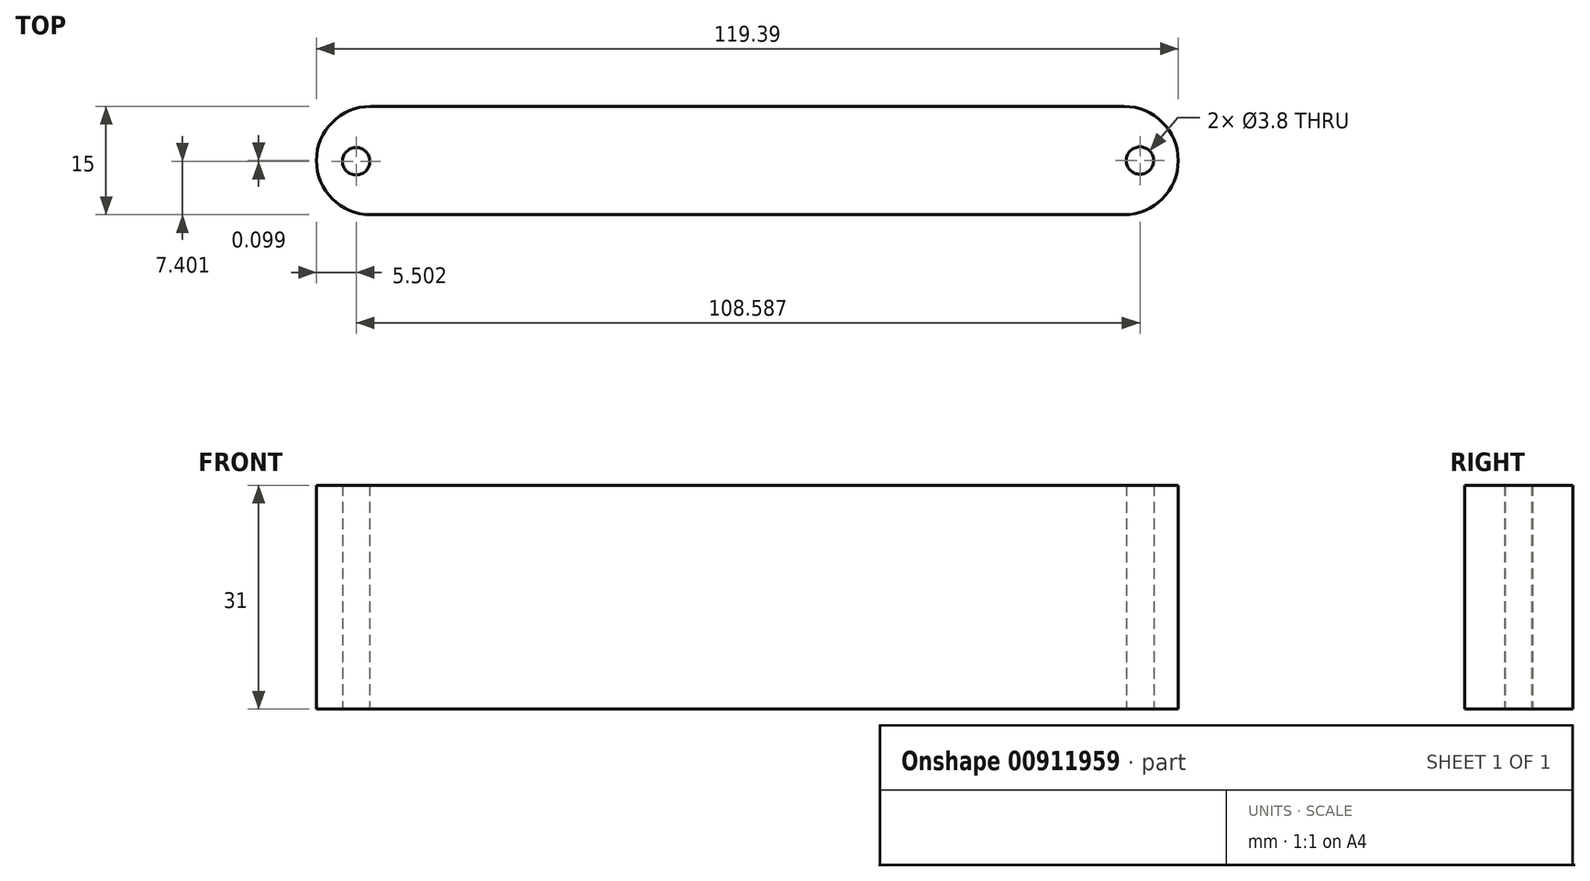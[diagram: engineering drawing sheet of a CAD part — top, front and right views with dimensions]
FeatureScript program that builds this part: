
annotation { "Feature Type Name" : "Feature", "Feature Type Description" : "" }
export const myFeature = defineFeature(function(context is Context, id is Id, definition is map)
    precondition{}
    {
        {
            var Q0;
            Q0=qCreatedBy(makeId("Front.planeOp"),FACE);
            var sketch = newSketch(context, id + "F0", { "sketchPlane" : qUnion([Q0])});
            skLineSegment(sketch, "E0.bottom", {"start": v(-92.62, 11.8) * mm, "end": v(27.38, 11.8) * mm});
            skLineSegment(sketch, "E0.top", {"start": v(-92.62, -19.2) * mm, "end": v(27.38, -19.2) * mm});
            skLineSegment(sketch, "E0.left", {"start": v(-92.62, 11.8) * mm, "end": v(-92.62, -19.2) * mm});
            skLineSegment(sketch, "E0.right", {"start": v(27.38, 11.8) * mm, "end": v(27.38, -19.2) * mm});
            skSolve(sketch);
        }
        {
            var Q0;
            Q0 = qSketchRegion(id + "F0", true);
            extrude(context, id + "F1", {"entities" : qUnion([Q0]), "depth" : 15 * mm, "offsetDistance" : 25 * mm});
        }
        {
            var Q0;
            Q0=makeQuery(id+"F1.opExtrude","SWEPT_FACE",FACE,{"disambiguationData":[OSD([sQuery(id+"F0.wireOp",EDGE,"E0.top")])]});
            var sketch = newSketch(context, id + "F2", { "sketchPlane" : qUnion([Q0])});
            skCircle(sketch, "E1", {"center": v(21.88, 7.5) * mm, "radius": 1.9 * mm});
            skSolve(sketch);
        }
        {
            var Q0;
            Q0 = qSketchRegion(id + "F2", true);
            extrude(context, id + "F3", {"entities" : qUnion([Q0]), "operationType" : NewBodyOperationType.REMOVE, "oppositeDirection" : true, "depth" : 60 * mm, "offsetDistance" : 25 * mm});
        }
        {
            var Q0;
            Q0=makeQuery(id+"F1.opExtrude","SWEPT_FACE",FACE,{"disambiguationData":[OSD([sQuery(id+"F0.wireOp",EDGE,"E0.top")])]});
            var sketch = newSketch(context, id + "F4", { "sketchPlane" : qUnion([Q0])});
            skArc(sketch, "E2", {"start": v(-84.7, 15) * mm, "mid": v(-92.2, 7.5) * mm, "end": v(-84.7, 0) * mm});
            skLineSegment(sketch, "E3", {"start": v(-84.7, 0) * mm, "end": v(-92.62, 0) * mm});
            skLineSegment(sketch, "E4", {"start": v(-92.62, 0) * mm, "end": v(-92.62, 15) * mm});
            skLineSegment(sketch, "E5", {"start": v(-92.62, 15) * mm, "end": v(-84.7, 15) * mm});
            skSolve(sketch);
        }
        {
            var Q0;
            Q0 = qSketchRegion(id + "F4", true);
            extrude(context, id + "F5", {"entities" : qUnion([Q0]), "operationType" : NewBodyOperationType.REMOVE, "oppositeDirection" : true, "depth" : 70 * mm, "offsetDistance" : 25 * mm});
        }
        {
            var Q0;
            Q0=makeQuery(id+"F1.opExtrude","SWEPT_FACE",FACE,{"disambiguationData":[OSD([sQuery(id+"F0.wireOp",EDGE,"E0.top")])]});
            var sketch = newSketch(context, id + "F6", { "sketchPlane" : qUnion([Q0])});
            skPoint(sketch, "E6.orphan", {"position": v(-92.2, 7.5) * mm});
            skCircle(sketch, "E7", {"center": v(-86.7, 7.6) * mm, "radius": 1.9 * mm});
            skSolve(sketch);
        }
        {
            var Q0;
            Q0 = qSketchRegion(id + "F6", true);
            extrude(context, id + "F7", {"entities" : qUnion([Q0]), "operationType" : NewBodyOperationType.REMOVE, "oppositeDirection" : true, "depth" : 80 * mm, "offsetDistance" : 25 * mm});
        }
        {
            var Q0;
            Q0=makeQuery(id+"F1.opExtrude","SWEPT_FACE",FACE,{"disambiguationData":[OSD([sQuery(id+"F0.wireOp",EDGE,"E0.top")])]});
            var sketch = newSketch(context, id + "F8", { "sketchPlane" : qUnion([Q0])});
            skArc(sketch, "E8", {"start": v(19.68, 0) * mm, "mid": v(27.18, 7.5) * mm, "end": v(19.68, 15) * mm});
            skLineSegment(sketch, "E9", {"start": v(19.68, 15) * mm, "end": v(27.38, 15) * mm});
            skLineSegment(sketch, "E10", {"start": v(27.38, 15) * mm, "end": v(27.38, 0) * mm});
            skLineSegment(sketch, "E11", {"start": v(27.38, 0) * mm, "end": v(19.68, 0) * mm});
            skSolve(sketch);
        }
        {
            var Q0;
            Q0 = qSketchRegion(id + "F8", true);
            extrude(context, id + "F9", {"entities" : qUnion([Q0]), "operationType" : NewBodyOperationType.REMOVE, "oppositeDirection" : true, "depth" : 70 * mm, "offsetDistance" : 25 * mm});
        }
    });
